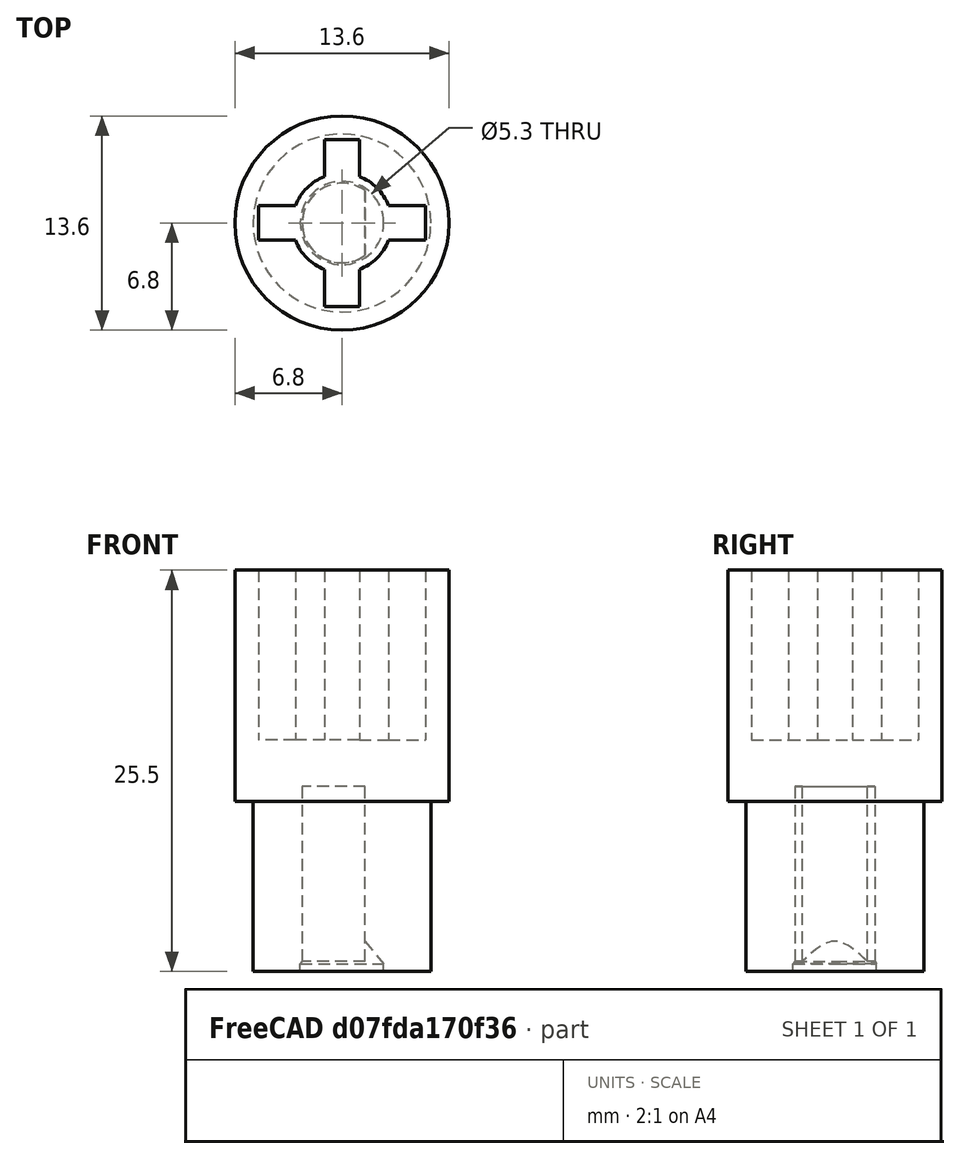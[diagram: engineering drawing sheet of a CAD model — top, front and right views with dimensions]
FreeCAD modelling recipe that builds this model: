
FCSTD DOCUMENT  (FreeCAD 1.0R38641 +678 (Git))
Label: Ambiano_coupling_V02
License: All rights reserved
LicenseURL: https://en.wikipedia.org/wiki/All_rights_reserved
objects: TechDraw::DrawViewDimension×5, Sketcher::SketchObject×4, TechDraw::DrawProjGroupItem×4, PartDesign::Pocket×3, PartDesign::Hole×2, PartDesign::Pad×1, PartDesign::SubtractiveCone×1, PartDesign::Body×1, TechDraw::DrawSVGTemplate×1, TechDraw::DrawProjGroup×1, TechDraw::DrawPage×1
note: 36 computed .brp shape members not serialized (recipe doc carries the construction recipe); baked Part::Feature solids carry a one-line shape summary decoded from their .brp

FEATURE [Sketcher::SketchObject] Sketch
  ArcFitTolerance = 1e-06
  AttachmentSupport = -> [XY_Plane]
  FullyConstrained = true
  MakeInternals = false
  MapMode = 5
  sketch-geometry (2):
    g0: Circle CenterX=0 CenterY=0 CenterZ=0 NormalX=0 NormalY=0 NormalZ=1 AngleXU=0 Radius=6.8
    g1: Circle CenterX=0 CenterY=0 CenterZ=0 NormalX=0 NormalY=0 NormalZ=1 AngleXU=0 Radius=5.65
  constraints (4):
    c: Diameter(g0) = 13.6
    c: Coincident(g0,g-1)
    c: Diameter(g1) = 11.3
    c: Coincident(g1,g0)
FEATURE [PartDesign::Pad] Pad
  Direction = (0,0,1)
  Length = 25.5
  Length2 = 10
  Profile = -> Sketch [Edge1]
  ReferenceAxis = -> Sketch [N_Axis]
  Refine = true
  Suppressed = false
  Type = 0
FEATURE [PartDesign::Pocket] Pocket
  BaseFeature = -> Pad
  Direction = (0,0,-1)
  Length = 10.8
  Length2 = 5
  Profile = -> Sketch [Edge2,Edge1]
  ReferenceAxis = -> Sketch [N_Axis]
  Refine = true
  Reversed = true
  Suppressed = false
  Type = 0
FEATURE [Sketcher::SketchObject] Sketch001
  ArcFitTolerance = 1e-06
  AttachmentSupport = -> [Pocket]
  FullyConstrained = true
  MakeInternals = false
  MapMode = 5
  Placement = pos=(0,0,0) rot=(1,0,0;3.14159rad)
  sketch-geometry (2):
    g0: ArcOfCircle CenterX=0 CenterY=0 CenterZ=0 NormalX=0 NormalY=0 NormalZ=1 AngleXU=0 Radius=2.525 StartAngle=0.947367 EndAngle=5.33582
    g1: LineSegment StartX=1.47415 StartY=2.05 StartZ=0 EndX=1.47415 EndY=-2.05 EndZ=0
  constraints (6):
    c: Diameter(g0) = 5.05
    c: Coincident(g0,g-1)
    c: DistanceY(g1,g1) = 4.1
    c: Parallel(g1,g-2)
    c: Coincident(g0,g1)
    c: Coincident(g0,g1)
FEATURE [PartDesign::Pocket] Pocket001
  BaseFeature = -> Pocket
  Direction = (0,0,1)
  Length = 11.75
  Length2 = 5
  Profile = -> Sketch001
  ReferenceAxis = -> Sketch001 [N_Axis]
  Refine = true
  Suppressed = false
  Type = 0
  UseCustomVector = true
FEATURE [Sketcher::SketchObject] Sketch002
  ArcFitTolerance = 1e-06
  AttachmentSupport = -> [Pocket001]
  FullyConstrained = true
  MakeInternals = false
  MapMode = 5
  Placement = pos=(0,0,0) rot=(1,0,0;3.14159rad)
  sketch-geometry (1):
    g0: Circle CenterX=0 CenterY=0 CenterZ=0 NormalX=0 NormalY=0 NormalZ=1 AngleXU=0 Radius=2.65
  constraints (2):
    c: Coincident(g0,g-1)
    c: Diameter(g0) = 5.3
FEATURE [PartDesign::SubtractiveCone] Cone
  Angle = 360
  AttacherType = Attacher::AttachEngine3D
  AttachmentOffset = pos=(0,0,-2.5) rot=(0,0,1;0rad)
  AttachmentSupport = -> [Pocket001]
  BaseFeature = -> Pocket001
  Height = 2
  MapMode = 2
  Placement = pos=(0,0,2.5) rot=(0,1,0;3.14159rad)
  Radius1 = 1
  Radius2 = 2.65
  Refine = true
  Suppressed = false
FEATURE [PartDesign::Hole] Hole
  BaseFeature = -> Cone
  CustomThreadClearance = 0
  Depth = 0.5
  DepthType = 0
  Diameter = 5.3
  DrillForDepth = false
  DrillPoint = 0
  DrillPointAngle = 118
  HoleCutCountersinkAngle = 90
  HoleCutCustomValues = false
  HoleCutDepth = 0
  HoleCutDiameter = 6.1
  HoleCutType = 0
  ModelThread = false
  Placement = pos=(0,0,2.5) rot=(0,1,0;3.14159rad)
  Profile = -> Cone [Face5]
  Refine = true
  Suppressed = false
  Tapered = false
  TaperedAngle = 90
  ThreadClass = 0
  ThreadDepth = 0.5
  ThreadDepthType = 0
  ThreadDirection = 0
  ThreadFit = 0
  ThreadSize = 0
  ThreadType = 0
  Threaded = false
  UseCustomThreadClearance = false
FEATURE [Sketcher::SketchObject] Sketch003
  ArcFitTolerance = 1e-06
  AttachmentSupport = -> [Hole]
  FullyConstrained = true
  MakeInternals = false
  MapMode = 5
  Placement = pos=(5.6e-15,0,25.5) rot=(0,0,1;3.14159rad)
  sketch-geometry (8):
    g0: LineSegment StartX=-5.3 StartY=-1.1 StartZ=0 EndX=5.3 EndY=-1.1 EndZ=0
    g1: LineSegment StartX=5.3 StartY=-1.1 StartZ=0 EndX=5.3 EndY=1.1 EndZ=0
    g2: LineSegment StartX=5.3 StartY=1.1 StartZ=0 EndX=-5.3 EndY=1.1 EndZ=0
    g3: LineSegment StartX=-5.3 StartY=1.1 StartZ=0 EndX=-5.3 EndY=-1.1 EndZ=0
    g4: LineSegment StartX=-1.1 StartY=5.3 StartZ=0 EndX=-1.1 EndY=-5.3 EndZ=0
    g5: LineSegment StartX=-1.1 StartY=-5.3 StartZ=0 EndX=1.1 EndY=-5.3 EndZ=0
    g6: LineSegment StartX=1.1 StartY=-5.3 StartZ=0 EndX=1.1 EndY=5.3 EndZ=0
    g7: LineSegment StartX=1.1 StartY=5.3 StartZ=0 EndX=-1.1 EndY=5.3 EndZ=0
  constraints (25):
    c: Coincident(g0,g1)
    c: Coincident(g1,g2)
    c: Coincident(g2,g3)
    c: Coincident(g3,g0)
    c: Horizontal(g0)
    c: Horizontal(g2)
    c: Vertical(g1)
    c: Vertical(g3)
    c: Coincident(g4,g5)
    c: Coincident(g5,g6)
    c: Coincident(g6,g7)
    c: Coincident(g7,g4)
    c: Vertical(g4)
    c: Vertical(g6)
    c: Horizontal(g5)
    c: Horizontal(g7)
    c: Distance(g7,g7) = 2.2  'CrossWidth'
    c: DistanceY(g4,g4) = 10.6
    c: Distance(g4,g-2) = 1.1
    c: Distance(g-1,g7) = 5.3
    c: DistanceX(g2,g2) = 10.6
    c: Distance(g1,g1) = 2.2
    c: DistanceY(g-1,g2) = 1.1
    c: DistanceX(g7,g7) = 2.2
    c: Distance(g-2,g1) = 5.3
FEATURE [PartDesign::Pocket] Pocket002
  BaseFeature = -> Hole
  Direction = (0,0,-1)
  Length = 10.8
  Length2 = 5
  Placement = pos=(0,0,2.5) rot=(0,1,0;3.14159rad)
  Profile = -> Sketch003
  ReferenceAxis = -> Sketch003 [N_Axis]
  Refine = true
  Suppressed = false
  Type = 0
FEATURE [PartDesign::Hole] Hole001
  BaseFeature = -> Pocket002
  CustomThreadClearance = 0
  Depth = 10.8
  DepthType = 0
  Diameter = 6.3
  DrillForDepth = false
  DrillPoint = 0
  DrillPointAngle = 118
  HoleCutCountersinkAngle = 90
  HoleCutCustomValues = false
  HoleCutDepth = 0
  HoleCutDiameter = 0
  HoleCutType = 0
  ModelThread = false
  Placement = pos=(0,0,2.5) rot=(0,1,0;3.14159rad)
  Profile = -> Pocket002 [Face3]
  Refine = true
  Suppressed = false
  Tapered = false
  TaperedAngle = 90
  ThreadClass = 0
  ThreadDepth = 10.8
  ThreadDepthType = 0
  ThreadDirection = 0
  ThreadFit = 0
  ThreadSize = 0
  ThreadType = 0
  Threaded = false
  UseCustomThreadClearance = false
FEATURE [PartDesign::Body] Body
  AllowCompound = false
  Group = -> [Sketch,Pad,Pocket,Sketch001,Pocket001,Sketch002,Cone,Hole,Sketch003,Pocket002,Hole001]
  Origin = -> Origin
  Tip = -> Hole001
FEATURE [TechDraw::DrawProjGroupItem] ProjItem001  label="Bottom"
  CoarseView = false
  Direction = (0,0,-1)
  Focus = 100
  HardHidden = false
  IsoCount = 0
  IsoHidden = false
  IsoVisible = false
  LockPosition = false
  Perspective = false
  Rotation = 0
  RotationVector = (1,0,0)
  ScaleType = 0
  ScrubCount = 1
  SeamHidden = false
  SeamVisible = false
  SmoothHidden = false
  SmoothVisible = true
  Source = -> [Body]
  Type = 5
  X = 0
  XDirection = (1,0,0)
  Y = 34.55
FEATURE [TechDraw::DrawSVGTemplate] Template
  Height = 210
  Orientation = 1
  Template = /snap/freecad/1634/usr/share/Mod/TechDraw/Templates/A4_Landscape_blank.svg
  Width = 297
FEATURE [TechDraw::DrawProjGroupItem] View  label="Front"
  CoarseView = false
  Direction = (0,-1,0)
  Focus = 100
  HardHidden = false
  IsoCount = 0
  IsoHidden = false
  IsoVisible = false
  LockPosition = true
  Perspective = false
  Rotation = 0
  RotationVector = (1,0,0)
  ScaleType = 2
  ScrubCount = 1
  SeamHidden = false
  SeamVisible = false
  SmoothHidden = false
  SmoothVisible = true
  Source = -> [Body]
  Type = 0
  X = 0
  XDirection = (1,0,0)
  Y = 0
FEATURE [TechDraw::DrawProjGroupItem] ProjItem  label="Bottom001"
  CoarseView = false
  Direction = (0,0,-1)
  Focus = 100
  HardHidden = false
  IsoCount = 0
  IsoHidden = false
  IsoVisible = false
  LockPosition = false
  Perspective = false
  Rotation = 0
  RotationVector = (1,0,0)
  ScaleType = 0
  ScrubCount = 1
  SeamHidden = false
  SeamVisible = false
  SmoothHidden = false
  SmoothVisible = true
  Source = -> [Body]
  Type = 5
  X = 0
  XDirection = (1,0,0)
  Y = 44.55
FEATURE [TechDraw::DrawProjGroupItem] ProjItem002  label="Top"
  CoarseView = false
  Direction = (0,0,1)
  Focus = 100
  HardHidden = false
  IsoCount = 0
  IsoHidden = false
  IsoVisible = false
  LockPosition = false
  Perspective = false
  Rotation = 0
  RotationVector = (1,0,0)
  ScaleType = 0
  ScrubCount = 1
  SeamHidden = false
  SeamVisible = false
  SmoothHidden = false
  SmoothVisible = true
  Source = -> [Body]
  Type = 4
  X = 0
  XDirection = (1,0,0)
  Y = -44.55
FEATURE [TechDraw::DrawProjGroup] ProjGroup
  Anchor = -> View
  AutoDistribute = true
  LockPosition = false
  ProjectionType = 0
  Rotation = 0
  ScaleType = 0
  Source = -> [Body]
  Views = -> [View,ProjItem,ProjItem002]
  X = 148.5
  Y = 105
  spacingX = 15
  spacingY = 25
FEATURE [TechDraw::DrawViewDimension] Dimension
  AngleOverride = false
  Arbitrary = false
  ArbitraryTolerances = false
  BoxCorners = (2) [(-6.8,-12.75,-1e-07),(6.8,12.75,1e-07)]
  EqualTolerance = true
  ExtensionAngle = 0
  FormatSpec = %.2w
  FormatSpecOverTolerance = %+.2w
  FormatSpecUnderTolerance = %+.2w
  Inverted = false
  LineAngle = 0
  LockPosition = false
  MeasureType = 1
  OverTolerance = 0
  References2D = -> [View]
  Rotation = 0
  ScaleType = 0
  TheoreticalExact = false
  Type = 0
  UnderTolerance = 0
  X = 38.6786
  Y = 29.3486
FEATURE [TechDraw::DrawViewDimension] Dimension001
  AngleOverride = false
  Arbitrary = false
  ArbitraryTolerances = false
  BoxCorners = (2) [(-6.8,-12.75,-1e-07),(6.8,12.75,1e-07)]
  EqualTolerance = true
  ExtensionAngle = 0
  FormatSpec = %.2w
  FormatSpecOverTolerance = %+.2w
  FormatSpecUnderTolerance = %+.2w
  Inverted = false
  LineAngle = 0
  LockPosition = false
  MeasureType = 1
  OverTolerance = 0
  References2D = -> [View]
  Rotation = 0
  ScaleType = 0
  TheoreticalExact = false
  Type = 0
  UnderTolerance = 0
  X = 60.3422
  Y = 22.0778
FEATURE [TechDraw::DrawViewDimension] Dimension002
  AngleOverride = false
  Arbitrary = false
  ArbitraryTolerances = false
  BoxCorners = (2) [(-6.8,-12.75,-1e-07),(6.8,12.75,1e-07)]
  EqualTolerance = true
  ExtensionAngle = 0
  FormatSpec = %.2w
  FormatSpecOverTolerance = %+.2w
  FormatSpecUnderTolerance = %+.2w
  Inverted = false
  LineAngle = 0
  LockPosition = false
  MeasureType = 1
  OverTolerance = 0
  References2D = -> [View]
  Rotation = 0
  ScaleType = 0
  TheoreticalExact = false
  Type = 0
  UnderTolerance = 0
  X = 57.0789
  Y = -19.9317
FEATURE [TechDraw::DrawViewDimension] Dimension003
  AngleOverride = false
  Arbitrary = false
  ArbitraryTolerances = false
  BoxCorners = (2) [(-6.8,-12.75,-1e-07),(6.8,12.75,1e-07)]
  EqualTolerance = true
  ExtensionAngle = 0
  FormatSpec = %.2w
  FormatSpecOverTolerance = %+.2w
  FormatSpecUnderTolerance = %+.2w
  Inverted = false
  LineAngle = 0
  LockPosition = false
  MeasureType = 1
  OverTolerance = 0
  References2D = -> [View]
  Rotation = 0
  ScaleType = 0
  TheoreticalExact = false
  Type = 0
  UnderTolerance = 0
  X = -17.3716
  Y = -15.0845
FEATURE [TechDraw::DrawViewDimension] Dimension004
  AngleOverride = false
  Arbitrary = false
  ArbitraryTolerances = false
  BoxCorners = (2) [(-6.8,-6.8,0),(6.8,6.8,0)]
  EqualTolerance = true
  ExtensionAngle = 0
  FormatSpec = %.2w
  FormatSpecOverTolerance = %+.2w
  FormatSpecUnderTolerance = %+.2w
  Inverted = false
  LineAngle = 0
  LockPosition = false
  MeasureType = 1
  OverTolerance = 0
  References2D = -> [ProjItem002]
  Rotation = 0
  ScaleType = 0
  TheoreticalExact = false
  Type = 0
  UnderTolerance = 0
  X = -25.0432
  Y = -3.62186
FEATURE [TechDraw::DrawPage] Page
  KeepUpdated = true
  NextBalloonIndex = 1
  ProjectionType = 0
  Template = -> Template
  Views = -> [ProjGroup,Dimension,Dimension001,Dimension002,Dimension003,Dimension004]
